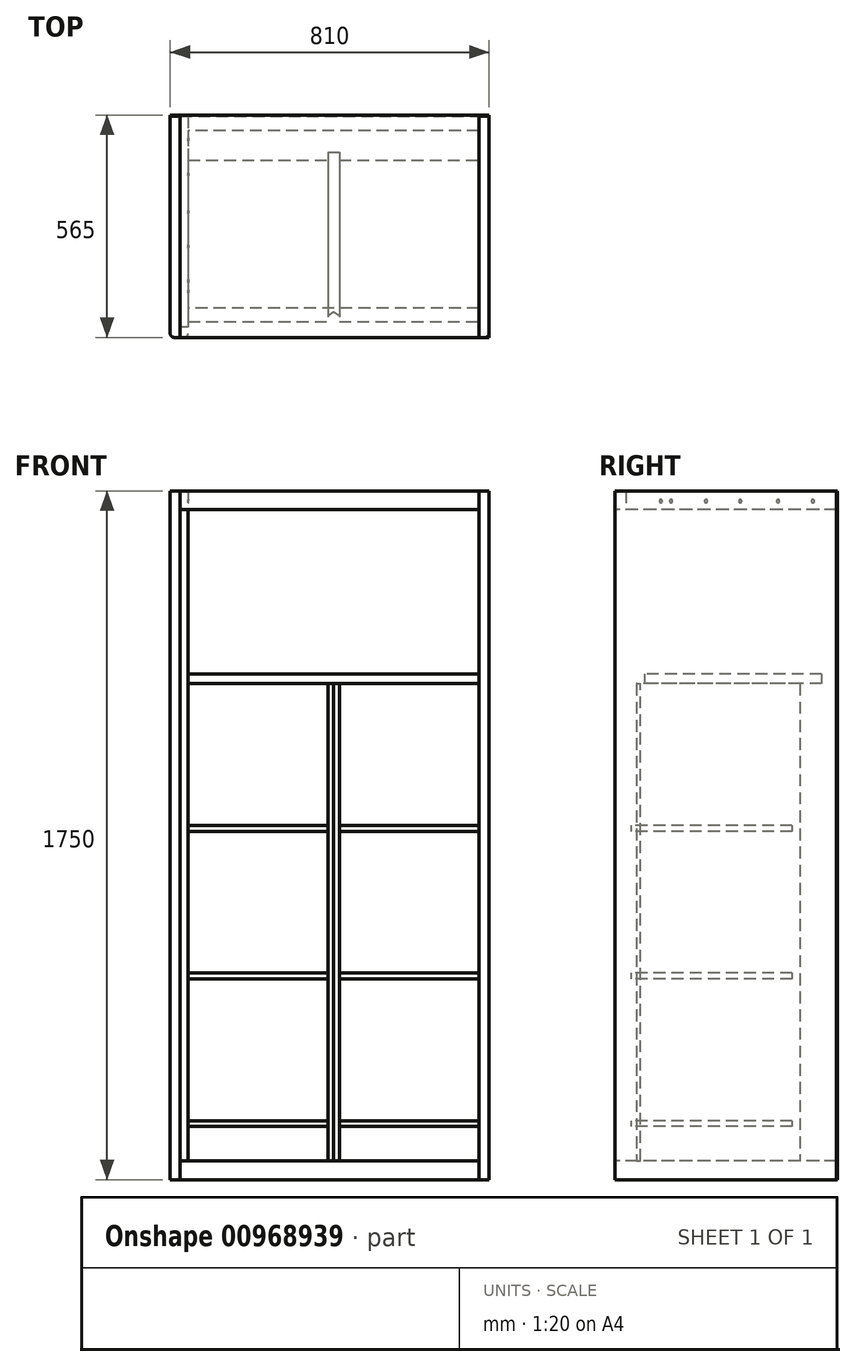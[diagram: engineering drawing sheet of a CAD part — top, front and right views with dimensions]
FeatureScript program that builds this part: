
annotation { "Feature Type Name" : "Feature", "Feature Type Description" : "" }
export const myFeature = defineFeature(function(context is Context, id is Id, definition is map)
    precondition{}
    {
        {
            var Q0;
            Q0=qCreatedBy(makeId("Front.planeOp"),FACE);
            var sketch = newSketch(context, id + "F0", { "sketchPlane" : qUnion([Q0])});
            skLineSegment(sketch, "E0.bottom", {"start": v(405, -875) * mm, "end": v(-405, -875) * mm});
            skLineSegment(sketch, "E0.top", {"start": v(405, 875) * mm, "end": v(-405, 875) * mm});
            skLineSegment(sketch, "E0.left", {"start": v(405, -875) * mm, "end": v(405, 875) * mm});
            skLineSegment(sketch, "E0.right", {"start": v(-405, -875) * mm, "end": v(-405, 875) * mm});
            skPoint(sketch, "E0.middle", {"position": v(0, 0) * mm});
            skLineSegment(sketch, "E1.bottom", {"start": v(-379.6, 828) * mm, "end": v(379.6, 828) * mm});
            skLineSegment(sketch, "E1.top", {"start": v(-379.6, -827) * mm, "end": v(379.6, -827) * mm});
            skLineSegment(sketch, "E1.left", {"start": v(-379.6, 828) * mm, "end": v(-379.6, -827) * mm});
            skLineSegment(sketch, "E1.right", {"start": v(379.6, 828) * mm, "end": v(379.6, -827) * mm});
            skLineSegment(sketch, "E2", {"start": v(-359.6, 385) * mm, "end": v(379.6, 385) * mm});
            skLineSegment(sketch, "E3", {"start": v(379.6, 410) * mm, "end": v(-359.6, 410) * mm});
            skLineSegment(sketch, "E4", {"start": v(-359.6, 828) * mm, "end": v(-359.6, -827) * mm});
            skLineSegment(sketch, "E5", {"start": v(-4.6, 385) * mm, "end": v(-4.6, -827) * mm});
            skLineSegment(sketch, "E6", {"start": v(24.6, 385) * mm, "end": v(24.6, -827) * mm});
            skLineSegment(sketch, "E7", {"start": v(-359.6, 25) * mm, "end": v(-4.6, 25) * mm});
            skLineSegment(sketch, "E8", {"start": v(-359.6, 10) * mm, "end": v(-4.6, 10) * mm});
            skLineSegment(sketch, "E9.0.1.0", {"start": v(-359.6, -350) * mm, "end": v(-4.6, -350) * mm});
            skLineSegment(sketch, "E9.0.1.1", {"start": v(-359.6, -365) * mm, "end": v(-4.6, -365) * mm});
            skLineSegment(sketch, "E9.0.2.0", {"start": v(-359.6, -725) * mm, "end": v(-4.6, -725) * mm});
            skLineSegment(sketch, "E9.0.2.1", {"start": v(-359.6, -740) * mm, "end": v(-4.6, -740) * mm});
            skLineSegment(sketch, "E9.1.0.0", {"start": v(24.6, 25) * mm, "end": v(379.6, 25) * mm});
            skLineSegment(sketch, "E9.1.0.1", {"start": v(24.6, 10) * mm, "end": v(379.6, 10) * mm});
            skLineSegment(sketch, "E9.1.1.0", {"start": v(24.6, -350) * mm, "end": v(379.6, -350) * mm});
            skLineSegment(sketch, "E9.1.1.1", {"start": v(24.6, -365) * mm, "end": v(379.6, -365) * mm});
            skLineSegment(sketch, "E9.1.2.0", {"start": v(24.6, -725) * mm, "end": v(379.6, -725) * mm});
            skLineSegment(sketch, "E9.1.2.1", {"start": v(24.6, -740) * mm, "end": v(379.6, -740) * mm});
            skLineSegment(sketch, "E9.direction1", {"start": v(-359.6, 25) * mm, "end": v(24.6, 25) * mm, "construction": true});
            skLineSegment(sketch, "E9.direction2", {"start": v(-359.6, 25) * mm, "end": v(-359.6, -350) * mm, "construction": true});
            skLineSegment(sketch, "E10", {"start": v(-379.6, 828) * mm, "end": v(-379.6, 875) * mm});
            skLineSegment(sketch, "E11", {"start": v(379.6, 828) * mm, "end": v(379.6, 875) * mm});
            skLineSegment(sketch, "E12", {"start": v(-379.6, -827) * mm, "end": v(-379.6, -875) * mm});
            skLineSegment(sketch, "E13", {"start": v(379.6, -827) * mm, "end": v(379.6, -875) * mm});
            skSolve(sketch);
        }
        {
            var Q0;
            {var subQ0=sQuery(id+"F0.wireOp",EDGE,"E10");Q0=makeQuery(id+"F0.imprint","IMPRINT",FACE,{"disambiguationData":[TD([[makeQuery(id+"F0.imprint","IMPRINT",EDGE,{"derivedFrom":subQ0}),-1.0]])]});}
            extrude(context, id + "F1", {"entities" : qUnion([Q0]), "oppositeDirection" : true, "depth" : 565 * mm, "offsetDistance" : 25 * mm});
        }
        {
            var Q0;
            {var subQ10=sQuery(id+"F0.wireOp",EDGE,"E0.left");Q0=makeQuery(id+"F0.imprint","IMPRINT",FACE,{"disambiguationData":[TD([[makeQuery(id+"F0.imprint","IMPRINT",EDGE,{"derivedFrom":subQ10}),1.0]])]});}
            extrude(context, id + "F2", {"entities" : qUnion([Q0]), "oppositeDirection" : true, "depth" : 565 * mm, "offsetDistance" : 25 * mm});
        }
        {
            var Q0;
            Q0=makeQuery(id+"F0.imprint","IMPRINT",FACE,{"disambiguationData":[TD([[makeQuery(id+"F0.imprint","IMPRINT",EDGE,{"derivedFrom":sQuery(id+"F0.wireOp",EDGE,"E0.bottom")}),-1.0]])]});
            extrude(context, id + "F3", {"entities" : qUnion([Q0]), "oppositeDirection" : true, "depth" : 565 * mm, "offsetDistance" : 25 * mm});
        }
        {
            var Q0;
            {var subQ3=sQuery(id+"F0.wireOp",EDGE,"E12");Q0=makeQuery(id+"F0.imprint","IMPRINT",FACE,{"disambiguationData":[TD([[makeQuery(id+"F0.imprint","IMPRINT",EDGE,{"derivedFrom":subQ3}),1.0]])]});}
            extrude(context, id + "F4", {"entities" : qUnion([Q0]), "oppositeDirection" : true, "depth" : 565 * mm, "offsetDistance" : 25 * mm});
        }
        {
            var Q0;
            {var subQ7=sQuery(id+"F0.wireOp",EDGE,"E3");Q0=makeQuery(id+"F0.imprint","IMPRINT",FACE,{"disambiguationData":[TD([[makeQuery(id+"F0.imprint","IMPRINT",EDGE,{"derivedFrom":subQ7}),1.0]])]});}
            extrude(context, id + "F5", {"entities" : qUnion([Q0]), "oppositeDirection" : true, "depth" : (75 + 450) * mm, "offsetDistance" : 25 * mm, "hasSecondDirection" : true, "secondDirectionOppositeDirection" : true, "secondDirectionDepth" : 75 * mm});
        }
        {
            var Q0;
            {var subQ4=sQuery(id+"F0.wireOp",EDGE,"E5");var subQ5=sQuery(id+"F0.wireOp",EDGE,"E1.top");var subQ6=makeQuery(id+"F0.imprint","INTERSECT",VERTEX,{"derivedFrom":[subQ5,subQ4]});Q0=makeQuery(id+"F0.imprint","IMPRINT",FACE,{"disambiguationData":[TD([[makeQuery(id+"F0.imprint","IMPRINT",EDGE,{"disambiguationData":[TD([[subQ6,-1.0]])],"derivedFrom":subQ5}),1.0]])]});}
            extrude(context, id + "F6", {"entities" : qUnion([Q0]), "oppositeDirection" : true, "depth" : 470 * mm, "offsetDistance" : 25 * mm, "hasSecondDirection" : true, "secondDirectionOppositeDirection" : true, "secondDirectionDepth" : 55 * mm});
        }
        {
            var Q0;
            {var subQ0=sQuery(id+"F0.wireOp",EDGE,"E7");Q0=makeQuery(id+"F0.imprint","IMPRINT",FACE,{"disambiguationData":[TD([[makeQuery(id+"F0.imprint","IMPRINT",EDGE,{"derivedFrom":subQ0}),-1.0]])]});}
            var Q1;
            {var subQ0=sQuery(id+"F0.wireOp",EDGE,"E9.1.0.0");Q1=makeQuery(id+"F0.imprint","IMPRINT",FACE,{"disambiguationData":[TD([[makeQuery(id+"F0.imprint","IMPRINT",EDGE,{"derivedFrom":subQ0}),-1.0]])]});}
            var Q2;
            {var subQ0=sQuery(id+"F0.wireOp",EDGE,"E9.0.1.0");Q2=makeQuery(id+"F0.imprint","IMPRINT",FACE,{"disambiguationData":[TD([[makeQuery(id+"F0.imprint","IMPRINT",EDGE,{"derivedFrom":subQ0}),-1.0]])]});}
            var Q3;
            {var subQ0=sQuery(id+"F0.wireOp",EDGE,"E9.1.1.0");Q3=makeQuery(id+"F0.imprint","IMPRINT",FACE,{"disambiguationData":[TD([[makeQuery(id+"F0.imprint","IMPRINT",EDGE,{"derivedFrom":subQ0}),-1.0]])]});}
            var Q4;
            {var subQ0=sQuery(id+"F0.wireOp",EDGE,"E9.1.2.0");Q4=makeQuery(id+"F0.imprint","IMPRINT",FACE,{"disambiguationData":[TD([[makeQuery(id+"F0.imprint","IMPRINT",EDGE,{"derivedFrom":subQ0}),-1.0]])]});}
            var Q5;
            {var subQ0=sQuery(id+"F0.wireOp",EDGE,"E9.0.2.0");Q5=makeQuery(id+"F0.imprint","IMPRINT",FACE,{"disambiguationData":[TD([[makeQuery(id+"F0.imprint","IMPRINT",EDGE,{"derivedFrom":subQ0}),-1.0]])]});}
            extrude(context, id + "F7", {"entities" : qUnion([Q0, Q1, Q2, Q3, Q4, Q5]), "oppositeDirection" : true, "depth" : (40 + 410) * mm, "offsetDistance" : 25 * mm, "hasSecondDirection" : true, "secondDirectionOppositeDirection" : true, "secondDirectionDepth" : 40 * mm});
        }
        {
            var Q0;
            {var subQ4=sQuery(id+"F0.wireOp",EDGE,"E1.left");Q0=makeQuery(id+"F0.imprint","IMPRINT",FACE,{"disambiguationData":[TD([[makeQuery(id+"F0.imprint","IMPRINT",EDGE,{"derivedFrom":subQ4}),1.0]])]});}
            extrude(context, id + "F8", {"entities" : qUnion([Q0]), "oppositeDirection" : true, "depth" : 562 * mm, "offsetDistance" : 25 * mm});
        }
        {
            var Q0;
            Q0=makeQuery(id+"F0.imprint","IMPRINT",FACE,{"disambiguationData":[TD([[makeQuery(id+"F0.imprint","IMPRINT",EDGE,{"derivedFrom":sQuery(id+"F0.wireOp",EDGE,"E0.bottom")}),-1.0]])]});
            var Q1;
            {var subQ4=sQuery(id+"F0.wireOp",EDGE,"E1.left");Q1=makeQuery(id+"F0.imprint","IMPRINT",FACE,{"disambiguationData":[TD([[makeQuery(id+"F0.imprint","IMPRINT",EDGE,{"derivedFrom":subQ4}),1.0]])]});}
            var Q2;
            {var subQ5=sQuery(id+"F0.wireOp",EDGE,"E3");Q2=makeQuery(id+"F0.imprint","IMPRINT",FACE,{"disambiguationData":[TD([[makeQuery(id+"F0.imprint","IMPRINT",EDGE,{"derivedFrom":subQ5}),-1.0]])]});}
            var Q3;
            {var subQ7=sQuery(id+"F0.wireOp",EDGE,"E3");Q3=makeQuery(id+"F0.imprint","IMPRINT",FACE,{"disambiguationData":[TD([[makeQuery(id+"F0.imprint","IMPRINT",EDGE,{"derivedFrom":subQ7}),1.0]])]});}
            var Q4;
            {var subQ5=sQuery(id+"F0.wireOp",EDGE,"E7");Q4=makeQuery(id+"F0.imprint","IMPRINT",FACE,{"disambiguationData":[TD([[makeQuery(id+"F0.imprint","IMPRINT",EDGE,{"derivedFrom":subQ5}),1.0]])]});}
            var Q5;
            {var subQ4=sQuery(id+"F0.wireOp",EDGE,"E5");var subQ5=sQuery(id+"F0.wireOp",EDGE,"E1.top");var subQ6=makeQuery(id+"F0.imprint","INTERSECT",VERTEX,{"derivedFrom":[subQ5,subQ4]});Q5=makeQuery(id+"F0.imprint","IMPRINT",FACE,{"disambiguationData":[TD([[makeQuery(id+"F0.imprint","IMPRINT",EDGE,{"disambiguationData":[TD([[subQ6,-1.0]])],"derivedFrom":subQ5}),1.0]])]});}
            var Q6;
            {var subQ3=sQuery(id+"F0.wireOp",EDGE,"E9.1.0.0");Q6=makeQuery(id+"F0.imprint","IMPRINT",FACE,{"disambiguationData":[TD([[makeQuery(id+"F0.imprint","IMPRINT",EDGE,{"derivedFrom":subQ3}),1.0]])]});}
            var Q7;
            {var subQ5=sQuery(id+"F0.wireOp",EDGE,"E9.0.2.1");Q7=makeQuery(id+"F0.imprint","IMPRINT",FACE,{"disambiguationData":[TD([[makeQuery(id+"F0.imprint","IMPRINT",EDGE,{"derivedFrom":subQ5}),-1.0]])]});}
            var Q8;
            {var subQ5=sQuery(id+"F0.wireOp",EDGE,"E9.1.2.1");Q8=makeQuery(id+"F0.imprint","IMPRINT",FACE,{"disambiguationData":[TD([[makeQuery(id+"F0.imprint","IMPRINT",EDGE,{"derivedFrom":subQ5}),-1.0]])]});}
            var Q9;
            {var subQ0=sQuery(id+"F0.wireOp",EDGE,"E9.1.2.0");Q9=makeQuery(id+"F0.imprint","IMPRINT",FACE,{"disambiguationData":[TD([[makeQuery(id+"F0.imprint","IMPRINT",EDGE,{"derivedFrom":subQ0}),-1.0]])]});}
            var Q10;
            {var subQ0=sQuery(id+"F0.wireOp",EDGE,"E9.0.2.0");Q10=makeQuery(id+"F0.imprint","IMPRINT",FACE,{"disambiguationData":[TD([[makeQuery(id+"F0.imprint","IMPRINT",EDGE,{"derivedFrom":subQ0}),-1.0]])]});}
            var Q11;
            {var subQ0=sQuery(id+"F0.wireOp",EDGE,"E9.0.1.1");Q11=makeQuery(id+"F0.imprint","IMPRINT",FACE,{"disambiguationData":[TD([[makeQuery(id+"F0.imprint","IMPRINT",EDGE,{"derivedFrom":subQ0}),-1.0]])]});}
            var Q12;
            {var subQ0=sQuery(id+"F0.wireOp",EDGE,"E9.1.1.1");Q12=makeQuery(id+"F0.imprint","IMPRINT",FACE,{"disambiguationData":[TD([[makeQuery(id+"F0.imprint","IMPRINT",EDGE,{"derivedFrom":subQ0}),-1.0]])]});}
            var Q13;
            {var subQ0=sQuery(id+"F0.wireOp",EDGE,"E9.1.1.0");Q13=makeQuery(id+"F0.imprint","IMPRINT",FACE,{"disambiguationData":[TD([[makeQuery(id+"F0.imprint","IMPRINT",EDGE,{"derivedFrom":subQ0}),-1.0]])]});}
            var Q14;
            {var subQ0=sQuery(id+"F0.wireOp",EDGE,"E9.0.1.0");Q14=makeQuery(id+"F0.imprint","IMPRINT",FACE,{"disambiguationData":[TD([[makeQuery(id+"F0.imprint","IMPRINT",EDGE,{"derivedFrom":subQ0}),-1.0]])]});}
            var Q15;
            {var subQ0=sQuery(id+"F0.wireOp",EDGE,"E8");Q15=makeQuery(id+"F0.imprint","IMPRINT",FACE,{"disambiguationData":[TD([[makeQuery(id+"F0.imprint","IMPRINT",EDGE,{"derivedFrom":subQ0}),-1.0]])]});}
            var Q16;
            {var subQ0=sQuery(id+"F0.wireOp",EDGE,"E9.1.0.1");Q16=makeQuery(id+"F0.imprint","IMPRINT",FACE,{"disambiguationData":[TD([[makeQuery(id+"F0.imprint","IMPRINT",EDGE,{"derivedFrom":subQ0}),-1.0]])]});}
            var Q17;
            {var subQ0=sQuery(id+"F0.wireOp",EDGE,"E7");Q17=makeQuery(id+"F0.imprint","IMPRINT",FACE,{"disambiguationData":[TD([[makeQuery(id+"F0.imprint","IMPRINT",EDGE,{"derivedFrom":subQ0}),-1.0]])]});}
            var Q18;
            {var subQ0=sQuery(id+"F0.wireOp",EDGE,"E9.1.0.0");Q18=makeQuery(id+"F0.imprint","IMPRINT",FACE,{"disambiguationData":[TD([[makeQuery(id+"F0.imprint","IMPRINT",EDGE,{"derivedFrom":subQ0}),-1.0]])]});}
            extrude(context, id + "F9", {"entities" : qUnion([Q0, Q1, Q2, Q3, Q4, Q5, Q6, Q7, Q8, Q9, Q10, Q11, Q12, Q13, Q14, Q15, Q16, Q17, Q18]), "oppositeDirection" : true, "depth" : 565 * mm, "offsetDistance" : 25 * mm, "hasSecondDirection" : true, "secondDirectionOppositeDirection" : true, "secondDirectionDepth" : (565 - 3) * mm});
        }
        {
            var Q0;
            Q0=makeQuery(id+"F3.opExtrude","CAP_EDGE",EDGE,{"disambiguationData":[OSD([sQuery(id+"F0.wireOp",EDGE,"E0.right")])],"isStart":true});
            var Q1;
            Q1=makeQuery(id+"F8.opExtrude","CAP_EDGE",EDGE,{"disambiguationData":[OSD([sQuery(id+"F0.wireOp",EDGE,"E4")])],"isStart":true});
            var Q2;
            Q2=makeQuery(id+"F2.opExtrude","CAP_EDGE",EDGE,{"disambiguationData":[OSD([sQuery(id+"F0.wireOp",EDGE,"E0.left")])],"isStart":true});
            fillet(context, id + "F10", {"entities" : qUnion([Q0, Q1, Q2]), "radius" : 10 * mm, "tangentPropagation" : true, "allowEdgeOverflow" : false});
        }
        {
            var Q0;
            Q0=makeQuery(id+"F6.opExtrude","SWEPT_FACE",FACE,{"disambiguationData":[OSD([sQuery(id+"F0.wireOp",EDGE,"E2")])]});
            var sketch = newSketch(context, id + "F11", { "sketchPlane" : qUnion([Q0]), "disableImprinting" : false});
            skLineSegment(sketch, "E14", {"start": v(10, 55) * mm, "end": v(10, 470) * mm, "construction": true});
            skLineSegment(sketch, "E15", {"start": v(-4.6, 55) * mm, "end": v(10, 65) * mm});
            skLineSegment(sketch, "E16", {"start": v(10, 65) * mm, "end": v(24.6, 55) * mm});
            skSolve(sketch);
        }
        {
            var Q0;
            Q0=makeQuery(id+"F11.imprint","IMPRINT",FACE,{"disambiguationData":[TD([[makeQuery(id+"F11.imprint","IMPRINT",EDGE,{"derivedFrom":sQuery(id+"F11.wireOp",EDGE,"E15")}),-1.0]])]});
            extrude(context, id + "F12", {"entities" : qUnion([Q0]), "operationType" : NewBodyOperationType.REMOVE, "oppositeDirection" : true, "depth" : 1212 * mm, "offsetDistance" : 25 * mm});
        }
        {
            var Q0;
            Q0=makeQuery(id+"F1.opExtrude","SWEPT_FACE",FACE,{"disambiguationData":[OSD([sQuery(id+"F0.wireOp",EDGE,"E1.bottom")])]});
            shell(context, id + "F13", {"entities" : qUnion([Q0]), "thickness" : 1 * mm});
        }
        {
            var Q0;
            Q0=makeQuery(id+"F8.opExtrude","SWEPT_FACE",FACE,{"disambiguationData":[OSD([sQuery(id+"F0.wireOp",EDGE,"E1.bottom")])]});
            var sketch = newSketch(context, id + "F14", { "sketchPlane" : qUnion([Q0])});
            skLineSegment(sketch, "E17.bottom", {"start": v(-379.6, 562) * mm, "end": v(-359.6, 562) * mm});
            skLineSegment(sketch, "E17.top", {"start": v(-379.6, 27.78) * mm, "end": v(-359.6, 27.78) * mm});
            skLineSegment(sketch, "E17.left", {"start": v(-379.6, 562) * mm, "end": v(-379.6, 27.78) * mm});
            skLineSegment(sketch, "E17.right", {"start": v(-359.6, 562) * mm, "end": v(-359.6, 27.78) * mm});
            skSolve(sketch);
        }
        {
            var Q0;
            Q0=makeQuery(id+"F14.imprint","IMPRINT",FACE,{"disambiguationData":[TD([[makeQuery(id+"F14.imprint","IMPRINT",EDGE,{"derivedFrom":sQuery(id+"F14.wireOp",EDGE,"E17.bottom")}),-1.0]])]});
            var Q1;
            Q1=makeQuery(id+"F13.opShell","OFFSET_FACE",FACE,{"disambiguationData":[OSD([sQuery(id+"F0.wireOp",EDGE,"E0.top")])]});
            extrude(context, id + "F15", {"entities" : qUnion([Q0]), "endBound" : BoundingType.UP_TO_SURFACE, "depth" : 25 * mm, "endBoundEntityFace" : qUnion([Q1]), "offsetDistance" : 25 * mm});
        }
        {
            var Q0;
            Q0=makeQuery(id+"F15.opExtrude","SWEPT_FACE",FACE,{"disambiguationData":[OSD([sQuery(id+"F14.wireOp",EDGE,"E17.right")])]});
            var sketch = newSketch(context, id + "F16", { "sketchPlane" : qUnion([Q0])});
            skCircle(sketch, "E18", {"center": v(116.35, 848.92) * mm, "radius": 3.85 * mm});
            skCircle(sketch, "E19", {"center": v(142.6, 848.92) * mm, "radius": 3.85 * mm});
            skCircle(sketch, "E20", {"center": v(231.27, 848.92) * mm, "radius": 3.85 * mm});
            skCircle(sketch, "E21", {"center": v(318.18, 848.92) * mm, "radius": 3.85 * mm});
            skCircle(sketch, "E22", {"center": v(414.23, 848.92) * mm, "radius": 3.85 * mm});
            skCircle(sketch, "E23", {"center": v(502.58, 848.92) * mm, "radius": 3.92 * mm});
            skSolve(sketch);
        }
        {
            var Q0;
            Q0=makeQuery(id+"F16.imprint","IMPRINT",FACE,{"disambiguationData":[TD([[makeQuery(id+"F16.imprint","IMPRINT",EDGE,{"derivedFrom":sQuery(id+"F16.wireOp",EDGE,"E18")}),1.0]])]});
            var Q1;
            Q1=makeQuery(id+"F16.imprint","IMPRINT",FACE,{"disambiguationData":[TD([[makeQuery(id+"F16.imprint","IMPRINT",EDGE,{"derivedFrom":sQuery(id+"F16.wireOp",EDGE,"E19")}),1.0]])]});
            var Q2;
            Q2=makeQuery(id+"F16.imprint","IMPRINT",FACE,{"disambiguationData":[TD([[makeQuery(id+"F16.imprint","IMPRINT",EDGE,{"derivedFrom":sQuery(id+"F16.wireOp",EDGE,"E20")}),1.0]])]});
            var Q3;
            Q3=makeQuery(id+"F16.imprint","IMPRINT",FACE,{"disambiguationData":[TD([[makeQuery(id+"F16.imprint","IMPRINT",EDGE,{"derivedFrom":sQuery(id+"F16.wireOp",EDGE,"E21")}),1.0]])]});
            var Q4;
            Q4=makeQuery(id+"F16.imprint","IMPRINT",FACE,{"disambiguationData":[TD([[makeQuery(id+"F16.imprint","IMPRINT",EDGE,{"derivedFrom":sQuery(id+"F16.wireOp",EDGE,"E22")}),1.0]])]});
            var Q5;
            Q5=makeQuery(id+"F16.imprint","IMPRINT",FACE,{"disambiguationData":[TD([[makeQuery(id+"F16.imprint","IMPRINT",EDGE,{"derivedFrom":sQuery(id+"F16.wireOp",EDGE,"E23")}),1.0]])]});
            extrude(context, id + "F17", {"entities" : qUnion([Q0, Q1, Q2, Q3, Q4, Q5]), "depth" : 1 * mm, "offsetDistance" : 25 * mm});
        }
        {
            var Q0;
            Q0=makeQuery(id+"F17.opExtrude","CAP_EDGE",EDGE,{"disambiguationData":[OSD([sQuery(id+"F16.wireOp",EDGE,"E18")])],"isStart":false});
            var Q1;
            Q1=makeQuery(id+"F17.opExtrude","CAP_EDGE",EDGE,{"disambiguationData":[OSD([sQuery(id+"F16.wireOp",EDGE,"E19")])],"isStart":false});
            var Q2;
            Q2=makeQuery(id+"F17.opExtrude","CAP_EDGE",EDGE,{"disambiguationData":[OSD([sQuery(id+"F16.wireOp",EDGE,"E20")])],"isStart":false});
            var Q3;
            Q3=makeQuery(id+"F17.opExtrude","CAP_EDGE",EDGE,{"disambiguationData":[OSD([sQuery(id+"F16.wireOp",EDGE,"E21")])],"isStart":false});
            var Q4;
            Q4=makeQuery(id+"F17.opExtrude","CAP_EDGE",EDGE,{"disambiguationData":[OSD([sQuery(id+"F16.wireOp",EDGE,"E22")])],"isStart":false});
            var Q5;
            Q5=makeQuery(id+"F17.opExtrude","CAP_FACE",FACE,{"disambiguationData":[OSD([sQuery(id+"F16.wireOp",EDGE,"E23")])],"isStart":false});
            fillet(context, id + "F18", {"entities" : qUnion([Q0, Q1, Q2, Q3, Q4, Q5]), "radius" : 1 * mm, "tangentPropagation" : true, "allowEdgeOverflow" : false});
        }
    });
